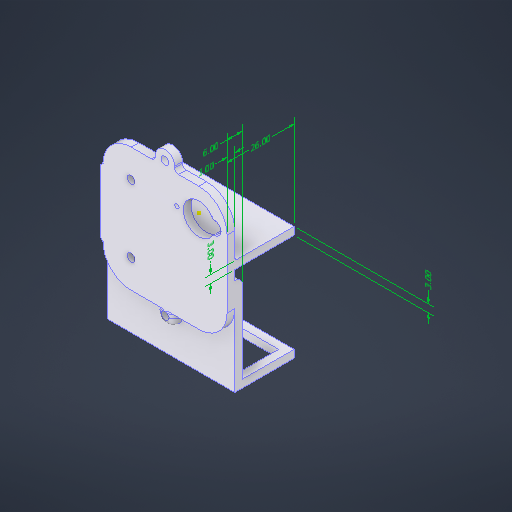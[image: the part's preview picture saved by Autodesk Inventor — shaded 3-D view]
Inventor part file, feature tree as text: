
AUTODESK INVENTOR PART (.ipt)
format: ipt  version: 2025.3 (Build 293356000, 356)  size: 420,352 bytes
history: native  units: in
note: dims shown in document units (in); Inventor stores cm internally (conversion verified against a paired STEP export)
features: extrude x12, sketch x10, other x6, fillet x5, direct_edit x3, move_body x3
ambient origin geometry x8: Origin, YZ Plane, XZ Plane, XY Plane, X Axis, Y Axis, Z Axis, Center Point
bodies: Solid1 (feature_tree)
feature tree (39):
  other  "Annotations"
  extrude  "Extrusion1"  Depth=0.0591in
  fillet  "Fillet1"  Radius=0.0591in
  fillet  "Fillet2"  Radius=0.9055in
  extrude  "Extrusion2"  Depth=1.0236in TaperAngle=0.0deg
  extrude  "Extrusion3"  Depth=0.0669in
  extrude  "Extrusion4"  Depth=1.172in
  fillet  "Fillet3"  Radius=1.0236in
  extrude  "Extrusion5"  Depth=0.1181in
  direct_edit  "Direct Edit1"
  extrude  "Extrusion6"  Depth=0.2378in
  extrude  "Extrusion7"  TaperAngle=0.0deg  [1 undecoded]
  direct_edit  "Direct Edit2"
  direct_edit  "Direct Edit3"
  sketch  "Sketch10"  dims[d25=0.0in d26=0.0in d27=0.6413in d28=0.1181in]
  extrude  "Extrusion8"  Depth=0.3937in TaperAngle=0.0deg
  extrude  "Extrusion9"  TaperAngle=0.0deg  [1 undecoded]
  extrude  "Extrusion10"  Depth=0.1181in
  extrude  "Extrusion11"  Depth=0.2362in TaperAngle=0.0deg
  fillet  "Fillet4"  [1 undecoded]
  extrude  "Extrusion12"  Depth=0.1181in
  fillet  "Fillet5"  Radius=0.1181in
  sketch  "Sketch1"  dims[d0=0.1181in d1=0.2953in d2=0.1181in d3=0.0in d4=0.0591in d5=0.0591in d11=0.9055in d12=0.0in]
  sketch  "Sketch2"  dims[d13=1.0236in d14=0.0in d17=1.0236in d18=0.0in]
  sketch  "Sketch3"  dims[d19=0.0315in d20=0.0669in]
  sketch  "Sketch7"  dims[d21=0.515in d22=1.172in d23=1.0236in d24=0.0in]
  sketch  "Sketch11"  dims[d29=0.4134in d30=0.2378in]
  sketch  "Sketch12"  dims[d31=0.3762in d32=0.0in d33=0.0in]
  sketch  "Sketch13"  dims[d34=0.1793in d35=0.3937in d36=0.0in]
  sketch  "Sketch14"  dims[d40=0.0in d41=0.0in d42=0.0394in d43=0.0in d44=0.0in d45=-0.0394in]
  sketch  "Sketch15"  dims[d50=0.1181in d51=0.0in d58=0.1181in d64=0.7874in d65=0.0in d66=45.0deg d67=0.1181in d68=0.1181in d69=135.0deg d70=0.7874in d71=0.0in d72=0.8504in d73=0.1181in d74=0.2362in d75=0.7874in d76=0.0in d77=0.1181in d78=0.1181in d79=0.7874in d80=0.0in d81=0.1181in d47=0.2862in d48=0.2809in d49=0.1181in d52=0.1865in d53=0.1902in d54=0.1181in d55=0.3167in d56=0.077in d57=0.1181in d59=0.0617in d60=0.0767in d61=0.2362in d62=0.158in d63=1.0236in]
  move_body  "Move1"
  move_body  "Move2"
  move_body  "Move3"
  other  "Linear Dimension 1"
  other  "Linear Dimension 2"
  other  "Linear Dimension 3"
  other  "Linear Dimension 4"
  other  "Linear Dimension 5"
note: 3 required parameter values undecoded (feature->parameter linkage not recoverable at this tier; creation-order binding heuristic only, values carry confidence <= 0.55)
